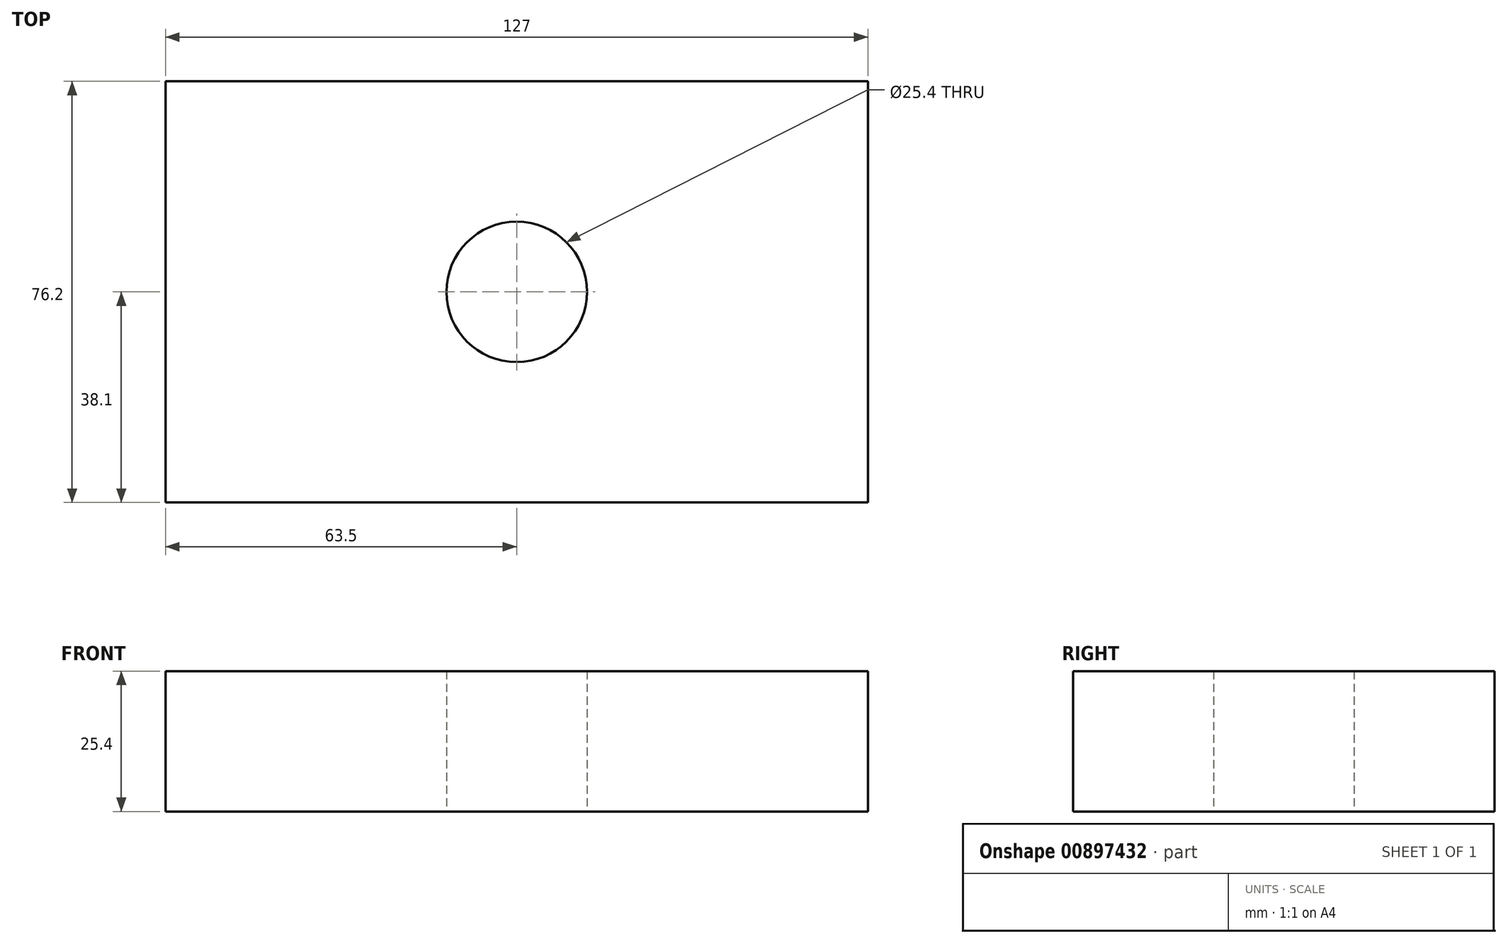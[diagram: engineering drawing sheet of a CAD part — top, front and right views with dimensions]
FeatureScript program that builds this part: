
annotation { "Feature Type Name" : "Feature", "Feature Type Description" : "" }
export const myFeature = defineFeature(function(context is Context, id is Id, definition is map)
    precondition{}
    {
        {
            var Q0;
            Q0=qCreatedBy(makeId("Top.planeOp"),FACE);
            var sketch = newSketch(context, id + "F0", { "sketchPlane" : qUnion([Q0])});
            skLineSegment(sketch, "E0.bottom", {"start": v(63.5, 38.1) * mm, "end": v(-63.5, 38.1) * mm});
            skLineSegment(sketch, "E0.top", {"start": v(63.5, -38.1) * mm, "end": v(-63.5, -38.1) * mm});
            skLineSegment(sketch, "E0.left", {"start": v(63.5, 38.1) * mm, "end": v(63.5, -38.1) * mm});
            skLineSegment(sketch, "E0.right", {"start": v(-63.5, 38.1) * mm, "end": v(-63.5, -38.1) * mm});
            skPoint(sketch, "E0.middle", {"position": v(0, 0) * mm});
            skCircle(sketch, "E1", {"center": v(0, 0) * mm, "radius": 12.7 * mm});
            skSolve(sketch);
        }
        {
            var Q0;
            Q0=makeQuery(id+"F0.imprint","IMPRINT",FACE,{"disambiguationData":[TD([[makeQuery(id+"F0.imprint","IMPRINT",EDGE,{"derivedFrom":sQuery(id+"F0.wireOp",EDGE,"E0.bottom")}),1.0]])]});
            var sketch = newSketch(context, id + "F1", { "sketchPlane" : qUnion([Q0])});
            skSolve(sketch);
        }
        {
            var Q0;
            Q0=makeQuery(id+"F1.imprint","IMPRINT",FACE,{"disambiguationData":[TD([[makeQuery(id+"F1.imprint","IMPRINT",EDGE,{"derivedFrom":makeQuery(id+"F0.imprint","IMPRINT",EDGE,{"derivedFrom":sQuery(id+"F0.wireOp",EDGE,"E0.bottom")})}),1.0]])]});
            extrude(context, id + "F2", {"entities" : qUnion([Q0]), "depth" : 25.4 * mm, "offsetDistance" : 25.4 * mm});
        }
    });
